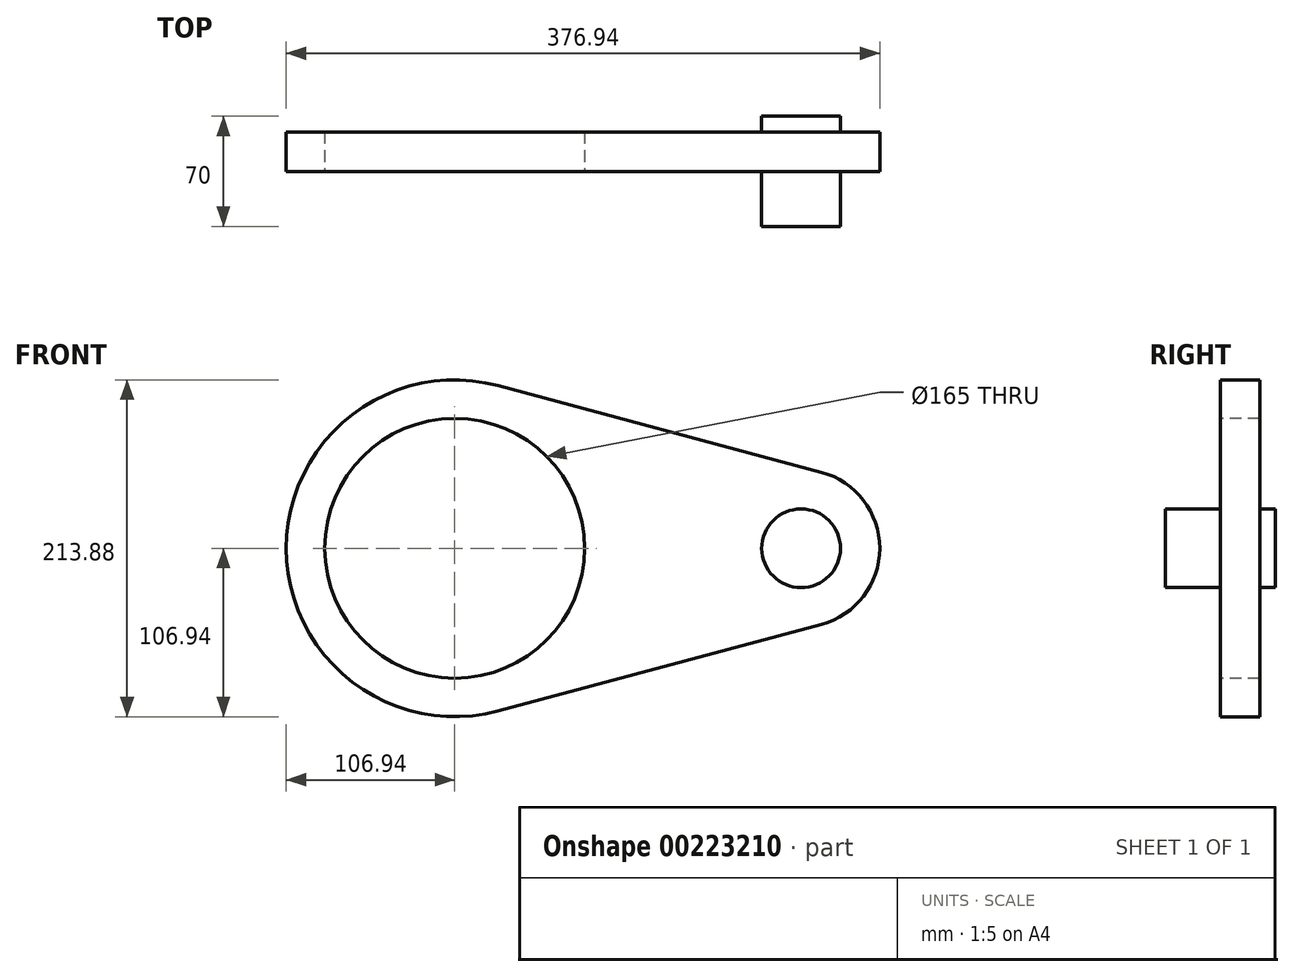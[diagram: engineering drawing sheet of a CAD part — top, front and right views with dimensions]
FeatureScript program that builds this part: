
annotation { "Feature Type Name" : "Feature", "Feature Type Description" : "" }
export const myFeature = defineFeature(function(context is Context, id is Id, definition is map)
    precondition{}
    {
        {
            var Q0;
            Q0=qCreatedBy(makeId("Front.planeOp"),FACE);
            var sketch = newSketch(context, id + "F0", { "sketchPlane" : qUnion([Q0])});
            skLineSegment(sketch, "E0", {"start": v(-85.94, 0) * mm, "end": v(83.09, 0) * mm, "construction": true});
            skLineSegment(sketch, "E1", {"start": v(-82.32, 103.3) * mm, "end": v(122.94, 48.3) * mm});
            skLineSegment(sketch, "E2.MirrorCS", {"start": v(-82.32, -103.3) * mm, "end": v(122.94, -48.3) * mm});
            skArc(sketch, "E3", {"start": v(122.94, 48.3) * mm, "mid": v(160, 0) * mm, "end": v(122.94, -48.3) * mm});
            skArc(sketch, "E4", {"start": v(-82.32, 103.3) * mm, "mid": v(-216.94, 0) * mm, "end": v(-82.32, -103.3) * mm});
            skCircle(sketch, "E5", {"center": v(110, 0) * mm, "radius": 25 * mm});
            skCircle(sketch, "E6", {"center": v(-110, 0) * mm, "radius": 82.5 * mm});
            skSolve(sketch);
        }
        {
            var Q0;
            Q0=makeQuery(id+"F0.imprint","IMPRINT",FACE,{"disambiguationData":[TD([[makeQuery(id+"F0.imprint","IMPRINT",EDGE,{"derivedFrom":sQuery(id+"F0.wireOp",EDGE,"E1")}),-1.0]])]});
            extrude(context, id + "F1", {"entities" : qUnion([Q0]), "oppositeDirection" : true, "depth" : 25 * mm});
        }
        {
            var Q0;
            Q0=makeQuery(id+"F0.imprint","IMPRINT",FACE,{"disambiguationData":[TD([[makeQuery(id+"F0.imprint","IMPRINT",EDGE,{"derivedFrom":sQuery(id+"F0.wireOp",EDGE,"E5")}),1.0]])]});
            extrude(context, id + "F2", {"entities" : qUnion([Q0]), "operationType" : NewBodyOperationType.ADD, "endBound" : BoundingType.SYMMETRIC, "depth" : 70 * mm});
        }
    });
